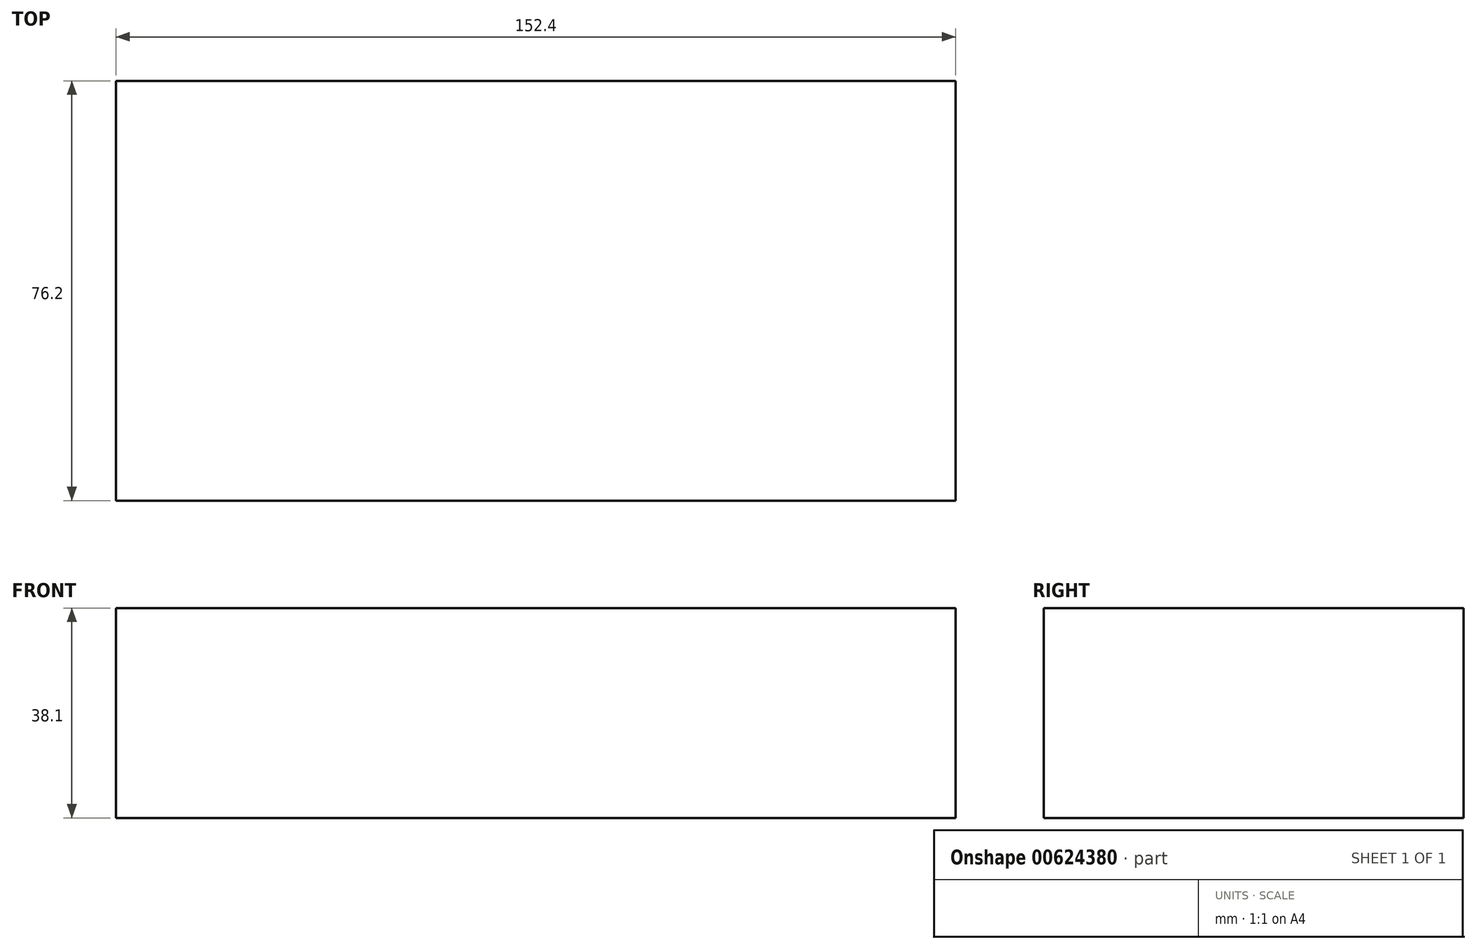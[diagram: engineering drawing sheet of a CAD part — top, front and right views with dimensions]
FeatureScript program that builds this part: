
annotation { "Feature Type Name" : "Feature", "Feature Type Description" : "" }
export const myFeature = defineFeature(function(context is Context, id is Id, definition is map)
    precondition{}
    {
        {
            var Q0;
            Q0=qCreatedBy(makeId("Top.planeOp"),FACE);
            var sketch = newSketch(context, id + "F0", { "sketchPlane" : qUnion([Q0])});
            skLineSegment(sketch, "E0.bottom", {"start": v(-66.61, 35.2) * mm, "end": v(85.79, 35.2) * mm});
            skLineSegment(sketch, "E0.top", {"start": v(-66.61, -41) * mm, "end": v(85.79, -41) * mm});
            skLineSegment(sketch, "E0.left", {"start": v(-66.61, 35.2) * mm, "end": v(-66.61, -41) * mm});
            skLineSegment(sketch, "E0.right", {"start": v(85.79, 35.2) * mm, "end": v(85.79, -41) * mm});
            skSolve(sketch);
        }
        {
            var Q0;
            Q0=makeQuery(id+"F0.imprint","IMPRINT",FACE,{"disambiguationData":[TD([[makeQuery(id+"F0.imprint","IMPRINT",EDGE,{"derivedFrom":sQuery(id+"F0.wireOp",EDGE,"E0.bottom")}),-1.0]])]});
            extrude(context, id + "F1", {"entities" : qUnion([Q0]), "depth" : 38.1 * mm, "offsetDistance" : 25.4 * mm});
        }
    });
